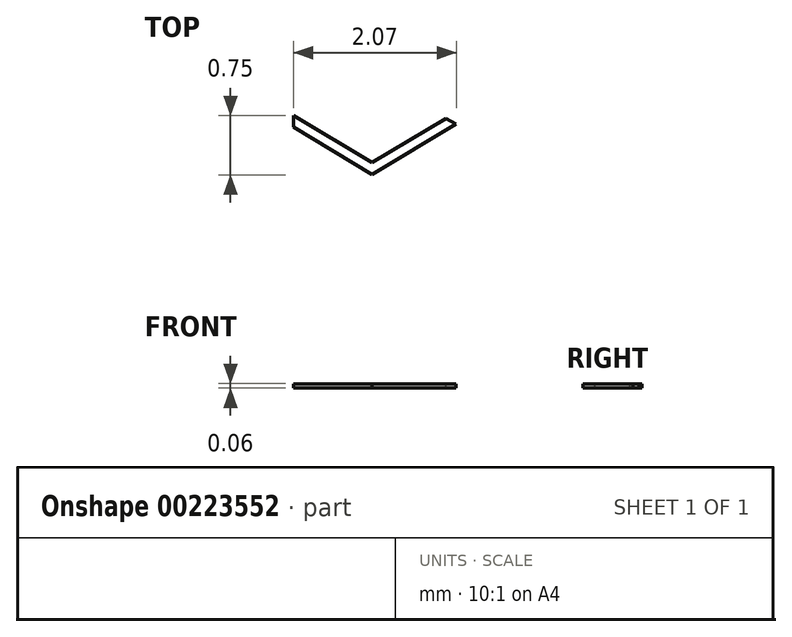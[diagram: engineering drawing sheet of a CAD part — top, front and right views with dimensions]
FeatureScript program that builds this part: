
annotation { "Feature Type Name" : "Feature", "Feature Type Description" : "" }
export const myFeature = defineFeature(function(context is Context, id is Id, definition is map)
    precondition{}
    {
        {
            var Q0;
            Q0=qCreatedBy(makeId("Top.planeOp"),FACE);
            var sketch = newSketch(context, id + "F0", { "sketchPlane" : qUnion([Q0])});
            skLineSegment(sketch, "E0.bottom", {"start": v(0, 0) * mm, "end": v(50, 0) * mm});
            skLineSegment(sketch, "E0.top", {"start": v(0, -50) * mm, "end": v(50, -50) * mm});
            skLineSegment(sketch, "E0.left", {"start": v(0, 0) * mm, "end": v(0, -50) * mm});
            skLineSegment(sketch, "E0.right", {"start": v(50, 0) * mm, "end": v(50, -50) * mm});
            skLineSegment(sketch, "E1", {"start": v(0, 0) * mm, "end": v(1, -0.6) * mm});
            skLineSegment(sketch, "E2", {"start": v(1, -0.6) * mm, "end": v(1, 0.87) * mm, "construction": true});
            skLineSegment(sketch, "E3.MirrorCS", {"start": v(2, 0) * mm, "end": v(1, -0.6) * mm});
            skLineSegment(sketch, "E4", {"start": v(0, -0.6) * mm, "end": v(2.27, -0.6) * mm, "construction": true});
            skLineSegment(sketch, "E5.MirrorCS", {"start": v(2, -1.2) * mm, "end": v(1, -0.6) * mm});
            skLineSegment(sketch, "E6.MirrorCS", {"start": v(0, -1.2) * mm, "end": v(1, -0.6) * mm});
            skSolve(sketch);
        }
        {
            var Q0;
            Q0=qCreatedBy(makeId("Right.planeOp"),FACE);
            var sketch = newSketch(context, id + "F1", { "sketchPlane" : qUnion([Q0])});
            skLineSegment(sketch, "E7.bottom", {"start": v(-0.07, -0.03) * mm, "end": v(0.07, -0.03) * mm});
            skLineSegment(sketch, "E7.top", {"start": v(-0.07, 0.03) * mm, "end": v(0.07, 0.03) * mm});
            skLineSegment(sketch, "E7.left", {"start": v(-0.07, -0.03) * mm, "end": v(-0.07, 0.03) * mm});
            skLineSegment(sketch, "E7.right", {"start": v(0.07, -0.02) * mm, "end": v(0.07, 0.03) * mm});
            skPoint(sketch, "E7.middle", {"position": v(0, 0) * mm});
            skSolve(sketch);
        }
        {
            var Q0;
            Q0=makeQuery(id+"F1.imprint","IMPRINT",FACE,{"disambiguationData":[TD([[makeQuery(id+"F1.imprint","IMPRINT",EDGE,{"derivedFrom":sQuery(id+"F1.wireOp",EDGE,"E7.bottom")}),1.0]])]});
            var Q1;
            Q1=sQuery(id+"F1.wireOp",EDGE,"E7.right");
            var Q2;
            Q2=sQuery(id+"F1.wireOp",EDGE,"E7.top");
            var Q3;
            Q3=sQuery(id+"F1.wireOp",EDGE,"E7.left");
            var Q4;
            Q4=sQuery(id+"F1.wireOp",EDGE,"E7.bottom");
            var Q5;
            Q5=sQuery(id+"F0.wireOp",EDGE,"E1");
            var Q6;
            Q6=sQuery(id+"F0.wireOp",EDGE,"E3.MirrorCS");
            sweep(context, id + "F2", {"bodyType" : ToolBodyType.SURFACE, "profiles" : qUnion([Q0]), "surfaceProfiles" : qUnion([Q1, Q2, Q3, Q4]), "path" : qUnion([Q5, Q6])});
        }
    });
